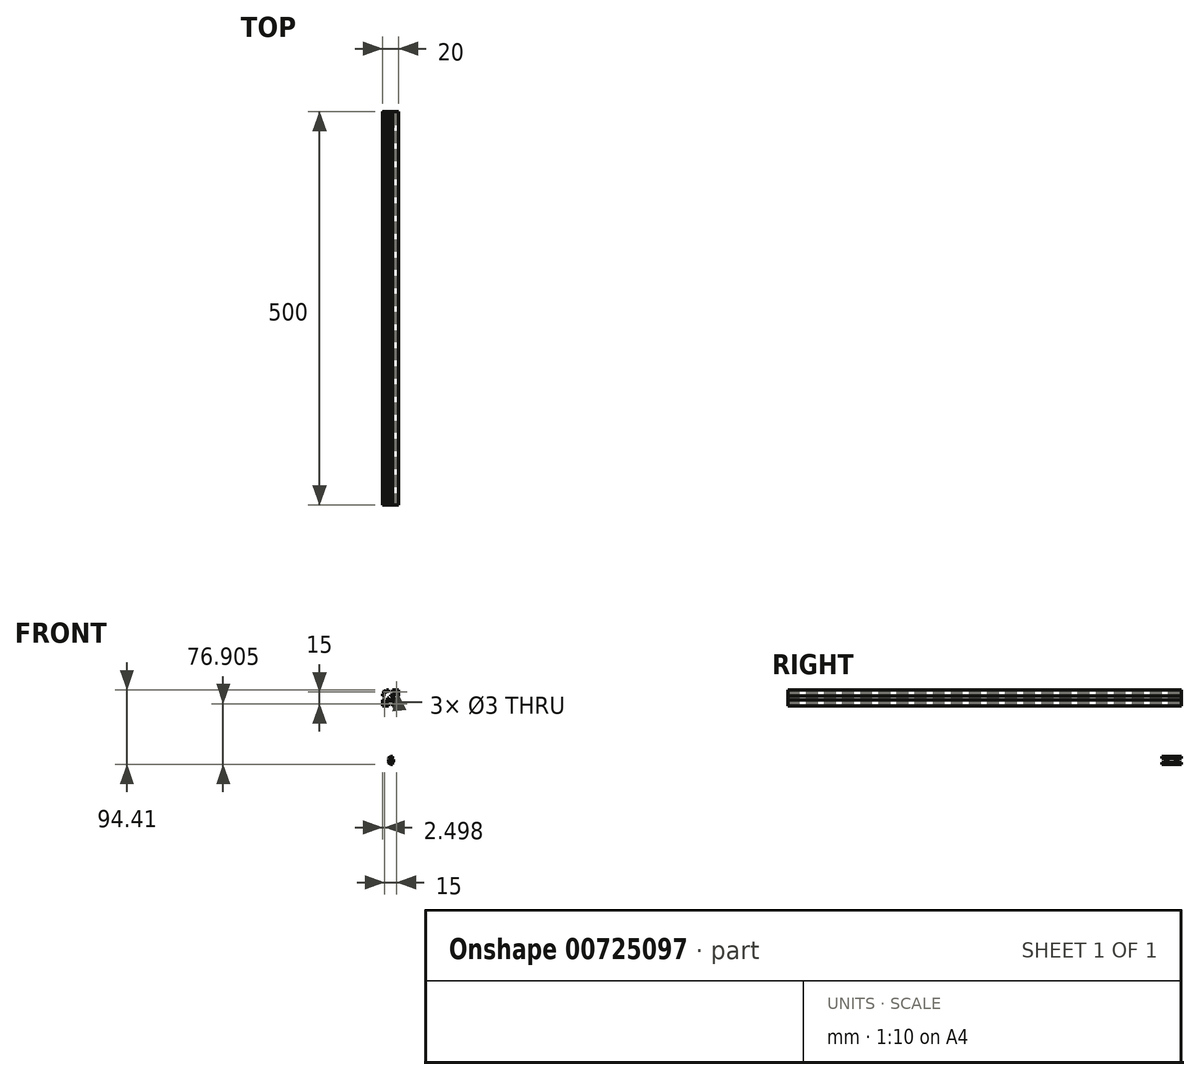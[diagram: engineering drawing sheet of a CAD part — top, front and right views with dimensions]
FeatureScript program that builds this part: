
annotation { "Feature Type Name" : "Feature", "Feature Type Description" : "" }
export const myFeature = defineFeature(function(context is Context, id is Id, definition is map)
    precondition{}
    {
        {
            var Q0;
            Q0=qCreatedBy(makeId("Front.planeOp"),FACE);
            var sketch = newSketch(context, id + "F0", { "sketchPlane" : qUnion([Q0])});
            skLineSegment(sketch, "E0.bottom", {"start": v(-63.67, 38.88) * mm, "end": v(-43.67, 38.88) * mm});
            skLineSegment(sketch, "E0.top", {"start": v(-63.67, 18.88) * mm, "end": v(-43.67, 18.88) * mm});
            skLineSegment(sketch, "E0.left", {"start": v(-63.67, 38.88) * mm, "end": v(-63.67, 18.88) * mm});
            skLineSegment(sketch, "E0.right", {"start": v(-43.67, 38.88) * mm, "end": v(-43.67, 18.88) * mm});
            skSolve(sketch);
        }
        {
            var Q0;
            Q0 = qSketchRegion(id + "F0", true);
            var Q1;
            Q1=makeQuery(id+"F0.imprint","IMPRINT",FACE,{"disambiguationData":[TD([[makeQuery(id+"F0.imprint","IMPRINT",EDGE,{"derivedFrom":sQuery(id+"F0.wireOp",EDGE,"E0.bottom")}),-1.0]])]});
            extrude(context, id + "F1", {"entities" : qUnion([Q0, Q1]), "depth" : 500 * mm, "offsetDistance" : 25 * mm});
        }
        {
            var Q0;
            Q0=makeQuery(id+"F1.opExtrude","CAP_FACE",FACE,{"disambiguationData":[OSD([sQuery(id+"F0.wireOp",EDGE,"E0.bottom"),sQuery(id+"F0.wireOp",EDGE,"E0.top"),sQuery(id+"F0.wireOp",EDGE,"E0.left"),sQuery(id+"F0.wireOp",EDGE,"E0.right")])],"isStart":true});
            var sketch = newSketch(context, id + "F2", { "sketchPlane" : qUnion([Q0])});
            skLineSegment(sketch, "E1", {"start": v(53.67, 32.71) * mm, "end": v(53.67, 28.88) * mm});
            skLineSegment(sketch, "E2", {"start": v(57.5, 28.88) * mm, "end": v(53.67, 28.88) * mm});
            skLineSegment(sketch, "E3", {"start": v(63.67, 28.88) * mm, "end": v(63.67, 23.88) * mm});
            skLineSegment(sketch, "E4.MirrorCS", {"start": v(63.67, 28.88) * mm, "end": v(63.67, 33.88) * mm});
            skLineSegment(sketch, "E5", {"start": v(63.67, 33.88) * mm, "end": v(59.67, 33.88) * mm});
            skLineSegment(sketch, "E6", {"start": v(59.67, 33.88) * mm, "end": v(57.5, 31.88) * mm});
            skLineSegment(sketch, "E7", {"start": v(57.5, 31.88) * mm, "end": v(57.5, 28.88) * mm});
            skLineSegment(sketch, "E8.MirrorCS", {"start": v(57.5, 25.88) * mm, "end": v(57.5, 28.88) * mm});
            skLineSegment(sketch, "E9.MirrorCS", {"start": v(59.67, 23.88) * mm, "end": v(57.5, 25.88) * mm});
            skLineSegment(sketch, "E10.MirrorCS", {"start": v(63.67, 23.88) * mm, "end": v(59.67, 23.88) * mm});
            skLineSegment(sketch, "E11", {"start": v(53.67, 28.88) * mm, "end": v(63.67, 18.88) * mm});
            skLineSegment(sketch, "E12.MirrorCS", {"start": v(58.67, 22.88) * mm, "end": v(56.67, 25.04) * mm});
            skLineSegment(sketch, "E13.MirrorCS", {"start": v(56.67, 25.04) * mm, "end": v(53.67, 25.04) * mm});
            skLineSegment(sketch, "E14.MirrorCS", {"start": v(58.67, 18.88) * mm, "end": v(58.67, 22.88) * mm});
            skLineSegment(sketch, "E15.MirrorCS", {"start": v(50.67, 25.04) * mm, "end": v(53.67, 25.04) * mm});
            skLineSegment(sketch, "E16.MirrorCS", {"start": v(48.67, 22.88) * mm, "end": v(50.67, 25.04) * mm});
            skLineSegment(sketch, "E17.MirrorCS", {"start": v(48.67, 18.88) * mm, "end": v(48.67, 22.88) * mm});
            skLineSegment(sketch, "E18", {"start": v(53.67, 28.88) * mm, "end": v(43.67, 38.88) * mm});
            skLineSegment(sketch, "E19.MirrorCS", {"start": v(49.83, 31.88) * mm, "end": v(49.83, 28.88) * mm});
            skLineSegment(sketch, "E20.MirrorCS", {"start": v(47.67, 33.88) * mm, "end": v(49.83, 31.88) * mm});
            skLineSegment(sketch, "E21.MirrorCS", {"start": v(43.67, 33.88) * mm, "end": v(47.67, 33.88) * mm});
            skLineSegment(sketch, "E22.MirrorCS", {"start": v(49.83, 25.88) * mm, "end": v(49.83, 28.88) * mm});
            skLineSegment(sketch, "E23.MirrorCS", {"start": v(47.67, 23.88) * mm, "end": v(49.83, 25.88) * mm});
            skLineSegment(sketch, "E24.MirrorCS", {"start": v(43.67, 23.88) * mm, "end": v(47.67, 23.88) * mm});
            skLineSegment(sketch, "E25.MirrorCS", {"start": v(50.67, 32.71) * mm, "end": v(53.67, 32.71) * mm});
            skLineSegment(sketch, "E26.MirrorCS", {"start": v(56.67, 32.71) * mm, "end": v(53.67, 32.71) * mm});
            skLineSegment(sketch, "E27.MirrorCS", {"start": v(58.67, 34.88) * mm, "end": v(56.67, 32.71) * mm});
            skLineSegment(sketch, "E28.MirrorCS", {"start": v(58.67, 38.88) * mm, "end": v(58.67, 34.88) * mm});
            skLineSegment(sketch, "E29.MirrorCS", {"start": v(48.67, 34.88) * mm, "end": v(50.67, 32.71) * mm});
            skLineSegment(sketch, "E30.MirrorCS", {"start": v(48.67, 38.88) * mm, "end": v(48.67, 34.88) * mm});
            skPoint(sketch, "E31.orphan", {"position": v(53.67, 38.88) * mm});
            skPoint(sketch, "E32.trimOffspring.end.orphan", {"position": v(43.67, 28.88) * mm});
            skPoint(sketch, "E33.trimOffspring.end.orphan", {"position": v(53.67, 18.88) * mm});
            skLineSegment(sketch, "E34", {"start": v(63.67, 38.88) * mm, "end": v(43.67, 18.88) * mm});
            skLineSegment(sketch, "E35", {"start": v(63.67, 23.88) * mm, "end": v(58.67, 18.88) * mm});
            skCircle(sketch, "E36", {"center": v(61.17, 21.38) * mm, "radius": 1.5 * mm});
            skCircle(sketch, "E37.MirrorC", {"center": v(46.17, 36.38) * mm, "radius": 1.5 * mm});
            skLineSegment(sketch, "E38", {"start": v(49.83, 28.88) * mm, "end": v(53.67, 28.88) * mm});
            skCircle(sketch, "E39.MirrorC", {"center": v(46.17, 21.38) * mm, "radius": 1.5 * mm});
            skCircle(sketch, "E40.MirrorC", {"center": v(61.17, 36.38) * mm, "radius": 1.5 * mm});
            skCircle(sketch, "E41", {"center": v(53.67, 28.88) * mm, "radius": 2.5 * mm});
            skLineSegment(sketch, "E42.bottom", {"start": v(48.67, 38.88) * mm, "end": v(51.17, 38.88) * mm});
            skLineSegment(sketch, "E42.top", {"start": v(48.67, 37.38) * mm, "end": v(51.17, 37.38) * mm});
            skLineSegment(sketch, "E42.left", {"start": v(48.67, 38.88) * mm, "end": v(48.67, 37.38) * mm});
            skLineSegment(sketch, "E42.right", {"start": v(51.17, 38.88) * mm, "end": v(51.17, 37.38) * mm});
            skLineSegment(sketch, "E43.MirrorCS", {"start": v(58.67, 37.38) * mm, "end": v(56.17, 37.38) * mm});
            skLineSegment(sketch, "E44.MirrorCS", {"start": v(56.17, 38.88) * mm, "end": v(56.17, 37.38) * mm});
            skLineSegment(sketch, "E45.MirrorCS", {"start": v(58.67, 38.88) * mm, "end": v(56.17, 38.88) * mm});
            skLineSegment(sketch, "E46.MirrorCS", {"start": v(58.67, 20.38) * mm, "end": v(56.17, 20.38) * mm});
            skLineSegment(sketch, "E47.MirrorCS", {"start": v(56.17, 18.88) * mm, "end": v(56.17, 20.38) * mm});
            skLineSegment(sketch, "E48.MirrorCS", {"start": v(51.17, 18.88) * mm, "end": v(51.17, 20.38) * mm});
            skLineSegment(sketch, "E49.MirrorCS", {"start": v(48.67, 20.38) * mm, "end": v(51.17, 20.38) * mm});
            skLineSegment(sketch, "E50.MirrorCS", {"start": v(45.17, 33.88) * mm, "end": v(45.17, 31.38) * mm});
            skLineSegment(sketch, "E51.MirrorCS", {"start": v(43.67, 31.38) * mm, "end": v(45.17, 31.38) * mm});
            skLineSegment(sketch, "E52.MirrorCS", {"start": v(43.67, 26.38) * mm, "end": v(45.17, 26.38) * mm});
            skLineSegment(sketch, "E53.MirrorCS", {"start": v(45.17, 23.88) * mm, "end": v(45.17, 26.38) * mm});
            skLineSegment(sketch, "E54.MirrorCS", {"start": v(63.67, 31.38) * mm, "end": v(62.17, 31.38) * mm});
            skLineSegment(sketch, "E55.MirrorCS", {"start": v(62.17, 33.88) * mm, "end": v(62.17, 31.38) * mm});
            skLineSegment(sketch, "E56.MirrorCS", {"start": v(63.67, 26.38) * mm, "end": v(62.17, 26.38) * mm});
            skLineSegment(sketch, "E57.MirrorCS", {"start": v(62.17, 23.88) * mm, "end": v(62.17, 26.38) * mm});
            skSolve(sketch);
        }
        {
            var Q0;
            Q0=makeQuery(id+"F2.imprint","IMPRINT",FACE,{"disambiguationData":[TD([[makeQuery(id+"F2.imprint","IMPRINT",EDGE,{"derivedFrom":sQuery(id+"F2.wireOp",EDGE,"E19.MirrorCS")}),-1.0]])]});
            var Q1;
            {var subQ4=sQuery(id+"F2.wireOp",EDGE,"E12.MirrorCS");Q1=makeQuery(id+"F2.imprint","IMPRINT",FACE,{"disambiguationData":[TD([[makeQuery(id+"F2.imprint","IMPRINT",EDGE,{"derivedFrom":subQ4}),1.0]])]});}
            var Q2;
            Q2=makeQuery(id+"F2.imprint","IMPRINT",FACE,{"disambiguationData":[TD([[makeQuery(id+"F2.imprint","IMPRINT",EDGE,{"derivedFrom":sQuery(id+"F2.wireOp",EDGE,"E8.MirrorCS")}),-1.0]])]});
            var Q3;
            Q3=makeQuery(id+"F2.imprint","IMPRINT",FACE,{"disambiguationData":[TD([[makeQuery(id+"F2.imprint","IMPRINT",EDGE,{"derivedFrom":sQuery(id+"F2.wireOp",EDGE,"E25.MirrorCS")}),1.0]])]});
            var Q4;
            {var subQ0=sQuery(id+"F2.wireOp",EDGE,"E40.MirrorC");var subQ1=sQuery(id+"F2.wireOp",EDGE,"E34");var subQ2=makeQuery(id+"F2.imprint","INTERSECT",VERTEX,{"disambiguationData":[OD(0.0)],"derivedFrom":[subQ1,subQ0]});Q4=makeQuery(id+"F2.imprint","IMPRINT",FACE,{"disambiguationData":[TD([[makeQuery(id+"F2.imprint","IMPRINT",EDGE,{"disambiguationData":[TD([[subQ2,-1.0]])],"derivedFrom":subQ1}),-1.0]])]});}
            var Q5;
            {var subQ0=sQuery(id+"F2.wireOp",EDGE,"E40.MirrorC");var subQ1=sQuery(id+"F2.wireOp",EDGE,"E34");var subQ2=makeQuery(id+"F2.imprint","INTERSECT",VERTEX,{"disambiguationData":[OD(0.0)],"derivedFrom":[subQ1,subQ0]});Q5=makeQuery(id+"F2.imprint","IMPRINT",FACE,{"disambiguationData":[TD([[makeQuery(id+"F2.imprint","IMPRINT",EDGE,{"disambiguationData":[TD([[subQ2,-1.0]])],"derivedFrom":subQ1}),1.0]])]});}
            var Q6;
            {var subQ1=sQuery(id+"F2.wireOp",EDGE,"E18");var subQ3=sQuery(id+"F2.wireOp",EDGE,"E41");var subQ4=makeQuery(id+"F2.imprint","INTERSECT",VERTEX,{"derivedFrom":[subQ1,subQ3]});Q6=makeQuery(id+"F2.imprint","IMPRINT",FACE,{"disambiguationData":[TD([[makeQuery(id+"F2.imprint","IMPRINT",EDGE,{"disambiguationData":[TD([[subQ4,-1.0]])],"derivedFrom":subQ3}),1.0]])]});}
            var Q7;
            {var subQ1=sQuery(id+"F2.wireOp",EDGE,"E34");var subQ3=sQuery(id+"F2.wireOp",EDGE,"E41");var subQ4=makeQuery(id+"F2.imprint","INTERSECT",VERTEX,{"disambiguationData":[OD(1.0)],"derivedFrom":[subQ1,subQ3]});Q7=makeQuery(id+"F2.imprint","IMPRINT",FACE,{"disambiguationData":[TD([[makeQuery(id+"F2.imprint","IMPRINT",EDGE,{"disambiguationData":[TD([[subQ4,1.0]])],"derivedFrom":subQ3}),1.0]])]});}
            var Q8;
            {var subQ1=sQuery(id+"F2.wireOp",EDGE,"E11");var subQ3=sQuery(id+"F2.wireOp",EDGE,"E41");var subQ4=makeQuery(id+"F2.imprint","INTERSECT",VERTEX,{"derivedFrom":[subQ1,subQ3]});Q8=makeQuery(id+"F2.imprint","IMPRINT",FACE,{"disambiguationData":[TD([[makeQuery(id+"F2.imprint","IMPRINT",EDGE,{"disambiguationData":[TD([[subQ4,1.0]])],"derivedFrom":subQ3}),1.0]])]});}
            var Q9;
            {var subQ1=sQuery(id+"F2.wireOp",EDGE,"E2");var subQ3=sQuery(id+"F2.wireOp",EDGE,"E41");var subQ4=makeQuery(id+"F2.imprint","INTERSECT",VERTEX,{"derivedFrom":[subQ1,subQ3]});Q9=makeQuery(id+"F2.imprint","IMPRINT",FACE,{"disambiguationData":[TD([[makeQuery(id+"F2.imprint","IMPRINT",EDGE,{"disambiguationData":[TD([[subQ4,1.0]])],"derivedFrom":subQ3}),1.0]])]});}
            var Q10;
            {var subQ1=sQuery(id+"F2.wireOp",EDGE,"E2");var subQ3=sQuery(id+"F2.wireOp",EDGE,"E41");var subQ4=makeQuery(id+"F2.imprint","INTERSECT",VERTEX,{"derivedFrom":[subQ1,subQ3]});Q10=makeQuery(id+"F2.imprint","IMPRINT",FACE,{"disambiguationData":[TD([[makeQuery(id+"F2.imprint","IMPRINT",EDGE,{"disambiguationData":[TD([[subQ4,-1.0]])],"derivedFrom":subQ3}),1.0]])]});}
            var Q11;
            {var subQ1=sQuery(id+"F2.wireOp",EDGE,"E1");var subQ3=sQuery(id+"F2.wireOp",EDGE,"E41");var subQ4=makeQuery(id+"F2.imprint","INTERSECT",VERTEX,{"derivedFrom":[subQ1,subQ3]});Q11=makeQuery(id+"F2.imprint","IMPRINT",FACE,{"disambiguationData":[TD([[makeQuery(id+"F2.imprint","IMPRINT",EDGE,{"disambiguationData":[TD([[subQ4,1.0]])],"derivedFrom":subQ3}),1.0]])]});}
            var Q12;
            {var subQ1=sQuery(id+"F2.wireOp",EDGE,"E1");var subQ3=sQuery(id+"F2.wireOp",EDGE,"E41");var subQ4=makeQuery(id+"F2.imprint","INTERSECT",VERTEX,{"derivedFrom":[subQ1,subQ3]});Q12=makeQuery(id+"F2.imprint","IMPRINT",FACE,{"disambiguationData":[TD([[makeQuery(id+"F2.imprint","IMPRINT",EDGE,{"disambiguationData":[TD([[subQ4,-1.0]])],"derivedFrom":subQ3}),1.0]])]});}
            var Q13;
            {var subQ0=sQuery(id+"F2.wireOp",EDGE,"E39.MirrorC");var subQ1=sQuery(id+"F2.wireOp",EDGE,"E34");var subQ2=makeQuery(id+"F2.imprint","INTERSECT",VERTEX,{"disambiguationData":[OD(0.0)],"derivedFrom":[subQ1,subQ0]});Q13=makeQuery(id+"F2.imprint","IMPRINT",FACE,{"disambiguationData":[TD([[makeQuery(id+"F2.imprint","IMPRINT",EDGE,{"disambiguationData":[TD([[subQ2,-1.0]])],"derivedFrom":subQ1}),-1.0]])]});}
            var Q14;
            {var subQ0=sQuery(id+"F2.wireOp",EDGE,"E39.MirrorC");var subQ1=sQuery(id+"F2.wireOp",EDGE,"E34");var subQ2=makeQuery(id+"F2.imprint","INTERSECT",VERTEX,{"disambiguationData":[OD(0.0)],"derivedFrom":[subQ1,subQ0]});Q14=makeQuery(id+"F2.imprint","IMPRINT",FACE,{"disambiguationData":[TD([[makeQuery(id+"F2.imprint","IMPRINT",EDGE,{"disambiguationData":[TD([[subQ2,-1.0]])],"derivedFrom":subQ1}),1.0]])]});}
            var Q15;
            {var subQ0=sQuery(id+"F2.wireOp",EDGE,"E36");var subQ1=sQuery(id+"F2.wireOp",EDGE,"E11");var subQ2=makeQuery(id+"F2.imprint","INTERSECT",VERTEX,{"disambiguationData":[OD(0.0)],"derivedFrom":[subQ1,subQ0]});Q15=makeQuery(id+"F2.imprint","IMPRINT",FACE,{"disambiguationData":[TD([[makeQuery(id+"F2.imprint","IMPRINT",EDGE,{"disambiguationData":[TD([[subQ2,-1.0]])],"derivedFrom":subQ1}),-1.0]])]});}
            var Q16;
            {var subQ0=sQuery(id+"F2.wireOp",EDGE,"E35");var subQ1=sQuery(id+"F2.wireOp",EDGE,"E11");var subQ2=makeQuery(id+"F2.imprint","INTERSECT",VERTEX,{"derivedFrom":[subQ1,subQ0]});Q16=makeQuery(id+"F2.imprint","IMPRINT",FACE,{"disambiguationData":[TD([[makeQuery(id+"F2.imprint","IMPRINT",EDGE,{"disambiguationData":[TD([[subQ2,-1.0]])],"derivedFrom":subQ1}),-1.0]])]});}
            var Q17;
            {var subQ0=sQuery(id+"F2.wireOp",EDGE,"E35");var subQ1=sQuery(id+"F2.wireOp",EDGE,"E11");var subQ2=makeQuery(id+"F2.imprint","INTERSECT",VERTEX,{"derivedFrom":[subQ1,subQ0]});Q17=makeQuery(id+"F2.imprint","IMPRINT",FACE,{"disambiguationData":[TD([[makeQuery(id+"F2.imprint","IMPRINT",EDGE,{"disambiguationData":[TD([[subQ2,-1.0]])],"derivedFrom":subQ1}),1.0]])]});}
            var Q18;
            {var subQ0=sQuery(id+"F2.wireOp",EDGE,"E36");var subQ1=sQuery(id+"F2.wireOp",EDGE,"E11");var subQ2=makeQuery(id+"F2.imprint","INTERSECT",VERTEX,{"disambiguationData":[OD(0.0)],"derivedFrom":[subQ1,subQ0]});Q18=makeQuery(id+"F2.imprint","IMPRINT",FACE,{"disambiguationData":[TD([[makeQuery(id+"F2.imprint","IMPRINT",EDGE,{"disambiguationData":[TD([[subQ2,-1.0]])],"derivedFrom":subQ1}),1.0]])]});}
            var Q19;
            {var subQ0=sQuery(id+"F2.wireOp",EDGE,"E37.MirrorC");var subQ1=sQuery(id+"F2.wireOp",EDGE,"E18");var subQ2=makeQuery(id+"F2.imprint","INTERSECT",VERTEX,{"disambiguationData":[OD(0.0)],"derivedFrom":[subQ1,subQ0]});Q19=makeQuery(id+"F2.imprint","IMPRINT",FACE,{"disambiguationData":[TD([[makeQuery(id+"F2.imprint","IMPRINT",EDGE,{"disambiguationData":[TD([[subQ2,-1.0]])],"derivedFrom":subQ1}),1.0]])]});}
            var Q20;
            {var subQ0=sQuery(id+"F2.wireOp",EDGE,"E37.MirrorC");var subQ1=sQuery(id+"F2.wireOp",EDGE,"E18");var subQ2=makeQuery(id+"F2.imprint","INTERSECT",VERTEX,{"disambiguationData":[OD(0.0)],"derivedFrom":[subQ1,subQ0]});Q20=makeQuery(id+"F2.imprint","IMPRINT",FACE,{"disambiguationData":[TD([[makeQuery(id+"F2.imprint","IMPRINT",EDGE,{"disambiguationData":[TD([[subQ2,-1.0]])],"derivedFrom":subQ1}),-1.0]])]});}
            extrude(context, id + "F3", {"entities" : qUnion([Q0, Q1, Q2, Q3, Q4, Q5, Q6, Q7, Q8, Q9, Q10, Q11, Q12, Q13, Q14, Q15, Q16, Q17, Q18, Q19, Q20]), "operationType" : NewBodyOperationType.REMOVE, "oppositeDirection" : true, "depth" : 500 * mm, "offsetDistance" : 25 * mm});
        }
        {
            var Q0;
            Q0=qCreatedBy(makeId("Front.planeOp"),FACE);
            var sketch = newSketch(context, id + "F4", { "sketchPlane" : qUnion([Q0])});
            skLineSegment(sketch, "E58", {"start": v(-49.8, -53.03) * mm, "end": v(-49.8, -48.03) * mm});
            skLineSegment(sketch, "E59", {"start": v(-49.8, -50.53) * mm, "end": v(-54.76, -50.53) * mm});
            skLineSegment(sketch, "E60", {"start": v(-49.8, -53.03) * mm, "end": v(-51.3, -53.03) * mm});
            skLineSegment(sketch, "E61", {"start": v(-51.3, -53.03) * mm, "end": v(-51.3, -55.53) * mm});
            skLineSegment(sketch, "E62", {"start": v(-51.3, -55.53) * mm, "end": v(-53.8, -55.53) * mm});
            skLineSegment(sketch, "E63", {"start": v(-53.8, -55.53) * mm, "end": v(-55.95, -53.53) * mm});
            skLineSegment(sketch, "E64", {"start": v(-55.95, -53.53) * mm, "end": v(-55.95, -50.53) * mm});
            skLineSegment(sketch, "E65.MirrorCS", {"start": v(-55.95, -47.53) * mm, "end": v(-55.95, -50.53) * mm});
            skLineSegment(sketch, "E66.MirrorCS", {"start": v(-53.8, -45.53) * mm, "end": v(-55.95, -47.53) * mm});
            skLineSegment(sketch, "E67.MirrorCS", {"start": v(-51.3, -45.53) * mm, "end": v(-53.8, -45.53) * mm});
            skLineSegment(sketch, "E68.MirrorCS", {"start": v(-51.3, -48.03) * mm, "end": v(-51.3, -45.53) * mm});
            skLineSegment(sketch, "E69.MirrorCS", {"start": v(-49.8, -48.03) * mm, "end": v(-51.3, -48.03) * mm});
            skSolve(sketch);
        }
        {
            var Q0;
            {var subQ0=sQuery(id+"F4.wireOp",EDGE,"E60");Q0=makeQuery(id+"F4.imprint","IMPRINT",FACE,{"disambiguationData":[TD([[makeQuery(id+"F4.imprint","IMPRINT",EDGE,{"derivedFrom":subQ0}),-1.0]])]});}
            extrude(context, id + "F5", {"entities" : qUnion([Q0]), "depth" : 25 * mm, "offsetDistance" : 25 * mm});
        }
        {
            var Q0;
            Q0=makeQuery(id+"F5.opExtrude","SWEPT_FACE",FACE,{"disambiguationData":[OSD([sQuery(id+"F4.wireOp",EDGE,"E58")])]});
            var sketch = newSketch(context, id + "F6", { "sketchPlane" : qUnion([Q0])});
            skLineSegment(sketch, "E70", {"start": v(-25, -50.53) * mm, "end": v(0, -50.53) * mm});
            skLineSegment(sketch, "E71", {"start": v(0, -50.53) * mm, "end": v(-6.25, -50.53) * mm});
            skLineSegment(sketch, "E72", {"start": v(-25, -50.53) * mm, "end": v(-18.75, -50.53) * mm});
            skCircle(sketch, "E73", {"center": v(-18.75, -50.53) * mm, "radius": 1.5 * mm});
            skCircle(sketch, "E74", {"center": v(-6.25, -50.53) * mm, "radius": 1.5 * mm});
            skSolve(sketch);
        }
        {
            var Q0;
            {var subQ0=sQuery(id+"F6.wireOp",EDGE,"E72");var subQ1=sQuery(id+"F6.wireOp",EDGE,"E70");var subQ2=makeQuery(id+"F6.imprint","INTERSECT",VERTEX,{"derivedFrom":[subQ1,subQ0]});Q0=makeQuery(id+"F6.imprint","IMPRINT",FACE,{"disambiguationData":[TD([[makeQuery(id+"F6.imprint","IMPRINT",EDGE,{"disambiguationData":[TD([[subQ2,-1.0]])],"derivedFrom":subQ1}),1.0]])]});}
            var Q1;
            {var subQ0=sQuery(id+"F6.wireOp",EDGE,"E72");var subQ1=sQuery(id+"F6.wireOp",EDGE,"E70");var subQ2=makeQuery(id+"F6.imprint","INTERSECT",VERTEX,{"derivedFrom":[subQ1,subQ0]});Q1=makeQuery(id+"F6.imprint","IMPRINT",FACE,{"disambiguationData":[TD([[makeQuery(id+"F6.imprint","IMPRINT",EDGE,{"disambiguationData":[TD([[subQ2,-1.0]])],"derivedFrom":subQ1}),-1.0]])]});}
            var Q2;
            {var subQ0=sQuery(id+"F6.wireOp",EDGE,"E71");var subQ1=sQuery(id+"F6.wireOp",EDGE,"E70");var subQ2=makeQuery(id+"F6.imprint","INTERSECT",VERTEX,{"derivedFrom":[subQ1,subQ0]});Q2=makeQuery(id+"F6.imprint","IMPRINT",FACE,{"disambiguationData":[TD([[makeQuery(id+"F6.imprint","IMPRINT",EDGE,{"disambiguationData":[TD([[subQ2,1.0]])],"derivedFrom":subQ1}),-1.0]])]});}
            var Q3;
            {var subQ0=sQuery(id+"F6.wireOp",EDGE,"E71");var subQ1=sQuery(id+"F6.wireOp",EDGE,"E70");var subQ2=makeQuery(id+"F6.imprint","INTERSECT",VERTEX,{"derivedFrom":[subQ1,subQ0]});Q3=makeQuery(id+"F6.imprint","IMPRINT",FACE,{"disambiguationData":[TD([[makeQuery(id+"F6.imprint","IMPRINT",EDGE,{"disambiguationData":[TD([[subQ2,1.0]])],"derivedFrom":subQ1}),1.0]])]});}
            extrude(context, id + "F7", {"entities" : qUnion([Q0, Q1, Q2, Q3]), "operationType" : NewBodyOperationType.REMOVE, "oppositeDirection" : true, "depth" : 25 * mm, "offsetDistance" : 25 * mm});
        }
    });
